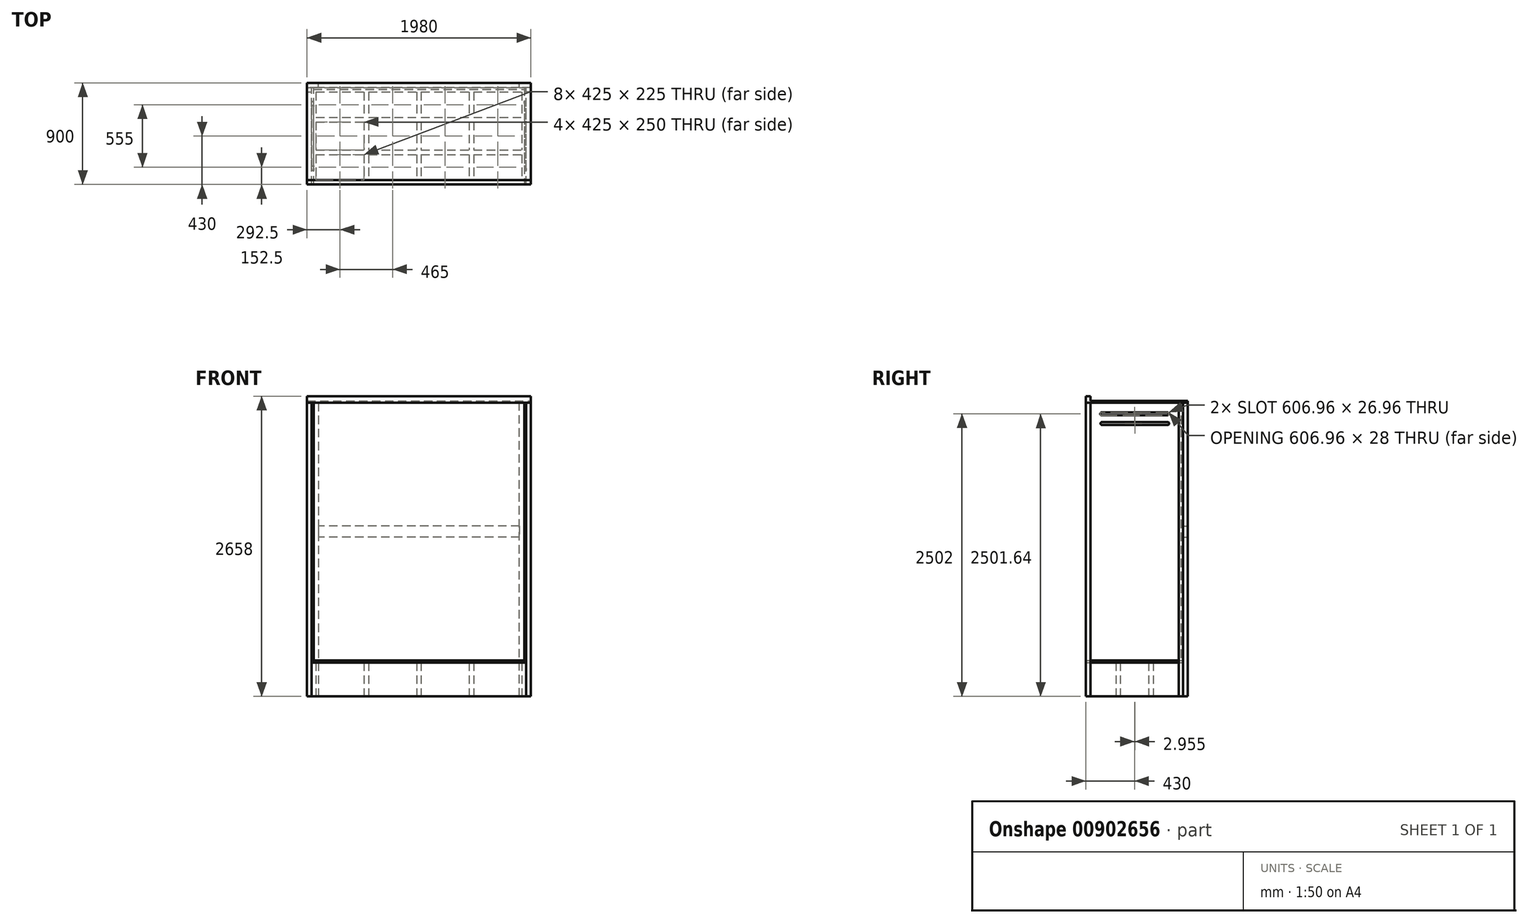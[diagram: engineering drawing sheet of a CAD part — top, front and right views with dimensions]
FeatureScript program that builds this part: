
annotation { "Feature Type Name" : "Feature", "Feature Type Description" : "" }
export const myFeature = defineFeature(function(context is Context, id is Id, definition is map)
    precondition{}
    {
        {
            var Q0;
            Q0=qCreatedBy(makeId("Top.planeOp"),FACE);
            var sketch = newSketch(context, id + "F0", { "sketchPlane" : qUnion([Q0])});
            skLineSegment(sketch, "E0.bottom", {"start": v(0, 0) * mm, "end": v(1900, 0) * mm});
            skLineSegment(sketch, "E0.top", {"start": v(0, 860) * mm, "end": v(1900, 860) * mm});
            skLineSegment(sketch, "E0.left", {"start": v(0, 0) * mm, "end": v(0, 860) * mm});
            skLineSegment(sketch, "E0.right", {"start": v(1900, 0) * mm, "end": v(1900, 860) * mm});
            skLineSegment(sketch, "E1.bottom", {"start": v(40, 820) * mm, "end": v(465, 820) * mm});
            skLineSegment(sketch, "E1.top", {"start": v(40, 40) * mm, "end": v(465, 40) * mm});
            skLineSegment(sketch, "E1.left", {"start": v(40, 820) * mm, "end": v(40, 595) * mm});
            skLineSegment(sketch, "E1.right", {"start": v(465, 820) * mm, "end": v(465, 595) * mm});
            skLineSegment(sketch, "E2.bottom", {"start": v(505, 820) * mm, "end": v(930, 820) * mm});
            skLineSegment(sketch, "E2.top", {"start": v(505, 40) * mm, "end": v(930, 40) * mm});
            skLineSegment(sketch, "E2.left", {"start": v(505, 820) * mm, "end": v(505, 595) * mm});
            skLineSegment(sketch, "E2.right", {"start": v(930, 820) * mm, "end": v(930, 595) * mm});
            skLineSegment(sketch, "E3.bottom", {"start": v(970, 820) * mm, "end": v(1395, 820) * mm});
            skLineSegment(sketch, "E3.top", {"start": v(970, 40) * mm, "end": v(1395, 40) * mm});
            skLineSegment(sketch, "E3.left", {"start": v(970, 820) * mm, "end": v(970, 595) * mm});
            skLineSegment(sketch, "E3.right", {"start": v(1395, 820) * mm, "end": v(1395, 595) * mm});
            skLineSegment(sketch, "E4.bottom", {"start": v(1435, 820) * mm, "end": v(1860, 820) * mm});
            skLineSegment(sketch, "E4.top", {"start": v(1435, 40) * mm, "end": v(1860, 40) * mm});
            skLineSegment(sketch, "E4.left", {"start": v(1435, 820) * mm, "end": v(1435, 595) * mm});
            skLineSegment(sketch, "E4.right", {"start": v(1860, 820) * mm, "end": v(1860, 595) * mm});
            skLineSegment(sketch, "E5.bottom", {"start": v(40, 595) * mm, "end": v(465, 595) * mm});
            skLineSegment(sketch, "E5.top", {"start": v(40, 555) * mm, "end": v(465, 555) * mm});
            skLineSegment(sketch, "E6.bottom", {"start": v(40, 265) * mm, "end": v(465, 265) * mm});
            skLineSegment(sketch, "E6.top", {"start": v(40, 305) * mm, "end": v(465, 305) * mm});
            skLineSegment(sketch, "E7.trimOffspring", {"start": v(505, 595) * mm, "end": v(930, 595) * mm});
            skLineSegment(sketch, "E8.trimOffspring", {"start": v(505, 555) * mm, "end": v(930, 555) * mm});
            skLineSegment(sketch, "E9.trimOffspring", {"start": v(465, 555) * mm, "end": v(465, 305) * mm});
            skLineSegment(sketch, "E10.trimOffspring", {"start": v(40, 555) * mm, "end": v(40, 305) * mm});
            skLineSegment(sketch, "E11.trimOffspring", {"start": v(505, 305) * mm, "end": v(930, 305) * mm});
            skLineSegment(sketch, "E12.trimOffspring", {"start": v(505, 265) * mm, "end": v(930, 265) * mm});
            skLineSegment(sketch, "E13.trimOffspring", {"start": v(970, 305) * mm, "end": v(1395, 305) * mm});
            skLineSegment(sketch, "E14.trimOffspring", {"start": v(970, 265) * mm, "end": v(1395, 265) * mm});
            skLineSegment(sketch, "E15.trimOffspring", {"start": v(970, 595) * mm, "end": v(1395, 595) * mm});
            skLineSegment(sketch, "E16.trimOffspring", {"start": v(970, 555) * mm, "end": v(1395, 555) * mm});
            skLineSegment(sketch, "E17.trimOffspring", {"start": v(1435, 595) * mm, "end": v(1860, 595) * mm});
            skLineSegment(sketch, "E18.trimOffspring", {"start": v(1435, 555) * mm, "end": v(1860, 555) * mm});
            skLineSegment(sketch, "E19.trimOffspring", {"start": v(1435, 305) * mm, "end": v(1860, 305) * mm});
            skLineSegment(sketch, "E20.trimOffspring", {"start": v(1435, 265) * mm, "end": v(1860, 265) * mm});
            skLineSegment(sketch, "E21.trimOffspring", {"start": v(505, 555) * mm, "end": v(505, 305) * mm});
            skLineSegment(sketch, "E22.trimOffspring", {"start": v(40, 265) * mm, "end": v(40, 40) * mm});
            skLineSegment(sketch, "E23.trimOffspring", {"start": v(465, 265) * mm, "end": v(465, 40) * mm});
            skLineSegment(sketch, "E24.trimOffspring", {"start": v(505, 265) * mm, "end": v(505, 40) * mm});
            skLineSegment(sketch, "E25.trimOffspring", {"start": v(930, 555) * mm, "end": v(930, 305) * mm});
            skLineSegment(sketch, "E26.trimOffspring", {"start": v(970, 555) * mm, "end": v(970, 305) * mm});
            skLineSegment(sketch, "E27.trimOffspring", {"start": v(970, 265) * mm, "end": v(970, 40) * mm});
            skLineSegment(sketch, "E28.trimOffspring", {"start": v(930, 265) * mm, "end": v(930, 40) * mm});
            skLineSegment(sketch, "E29.trimOffspring", {"start": v(1435, 265) * mm, "end": v(1435, 40) * mm});
            skLineSegment(sketch, "E30.trimOffspring", {"start": v(1395, 265) * mm, "end": v(1395, 40) * mm});
            skLineSegment(sketch, "E31.trimOffspring", {"start": v(1860, 265) * mm, "end": v(1860, 40) * mm});
            skLineSegment(sketch, "E32.trimOffspring", {"start": v(1860, 555) * mm, "end": v(1860, 305) * mm});
            skLineSegment(sketch, "E33.trimOffspring", {"start": v(1435, 555) * mm, "end": v(1435, 305) * mm});
            skLineSegment(sketch, "E34.trimOffspring", {"start": v(1395, 555) * mm, "end": v(1395, 305) * mm});
            skSolve(sketch);
        }
        {
            var Q0;
            Q0 = qSketchRegion(id + "F0", true);
            extrude(context, id + "F1", {"entities" : qUnion([Q0]), "depth" : 300 * mm, "offsetDistance" : 25 * mm});
        }
        {
            var Q0;
            Q0=makeQuery(id+"F1.opExtrude","CAP_FACE",FACE,{"disambiguationData":[OSD([sQuery(id+"F0.wireOp",EDGE,"E0.bottom"),sQuery(id+"F0.wireOp",EDGE,"E0.top"),sQuery(id+"F0.wireOp",EDGE,"E0.left"),sQuery(id+"F0.wireOp",EDGE,"E0.right"),sQuery(id+"F0.wireOp",EDGE,"E1.bottom"),sQuery(id+"F0.wireOp",EDGE,"E1.top"),sQuery(id+"F0.wireOp",EDGE,"E1.left"),sQuery(id+"F0.wireOp",EDGE,"E1.right"),sQuery(id+"F0.wireOp",EDGE,"E2.bottom"),sQuery(id+"F0.wireOp",EDGE,"E2.top"),sQuery(id+"F0.wireOp",EDGE,"E2.left"),sQuery(id+"F0.wireOp",EDGE,"E2.right"),sQuery(id+"F0.wireOp",EDGE,"E3.bottom"),sQuery(id+"F0.wireOp",EDGE,"E3.top"),sQuery(id+"F0.wireOp",EDGE,"E3.left"),sQuery(id+"F0.wireOp",EDGE,"E3.right"),sQuery(id+"F0.wireOp",EDGE,"E4.bottom"),sQuery(id+"F0.wireOp",EDGE,"E4.top"),sQuery(id+"F0.wireOp",EDGE,"E4.left"),sQuery(id+"F0.wireOp",EDGE,"E4.right"),sQuery(id+"F0.wireOp",EDGE,"E5.bottom"),sQuery(id+"F0.wireOp",EDGE,"E5.top"),sQuery(id+"F0.wireOp",EDGE,"E6.bottom"),sQuery(id+"F0.wireOp",EDGE,"E6.top"),sQuery(id+"F0.wireOp",EDGE,"E7.trimOffspring"),sQuery(id+"F0.wireOp",EDGE,"E8.trimOffspring"),sQuery(id+"F0.wireOp",EDGE,"E9.trimOffspring"),sQuery(id+"F0.wireOp",EDGE,"E10.trimOffspring"),sQuery(id+"F0.wireOp",EDGE,"E11.trimOffspring"),sQuery(id+"F0.wireOp",EDGE,"E12.trimOffspring"),sQuery(id+"F0.wireOp",EDGE,"E13.trimOffspring"),sQuery(id+"F0.wireOp",EDGE,"E14.trimOffspring"),sQuery(id+"F0.wireOp",EDGE,"E15.trimOffspring"),sQuery(id+"F0.wireOp",EDGE,"E16.trimOffspring"),sQuery(id+"F0.wireOp",EDGE,"E17.trimOffspring"),sQuery(id+"F0.wireOp",EDGE,"E18.trimOffspring"),sQuery(id+"F0.wireOp",EDGE,"E19.trimOffspring"),sQuery(id+"F0.wireOp",EDGE,"E20.trimOffspring"),sQuery(id+"F0.wireOp",EDGE,"E21.trimOffspring"),sQuery(id+"F0.wireOp",EDGE,"E22.trimOffspring"),sQuery(id+"F0.wireOp",EDGE,"E23.trimOffspring"),sQuery(id+"F0.wireOp",EDGE,"E24.trimOffspring"),sQuery(id+"F0.wireOp",EDGE,"E25.trimOffspring"),sQuery(id+"F0.wireOp",EDGE,"E26.trimOffspring"),sQuery(id+"F0.wireOp",EDGE,"E27.trimOffspring"),sQuery(id+"F0.wireOp",EDGE,"E28.trimOffspring"),sQuery(id+"F0.wireOp",EDGE,"E29.trimOffspring"),sQuery(id+"F0.wireOp",EDGE,"E30.trimOffspring"),sQuery(id+"F0.wireOp",EDGE,"E31.trimOffspring"),sQuery(id+"F0.wireOp",EDGE,"E32.trimOffspring"),sQuery(id+"F0.wireOp",EDGE,"E33.trimOffspring"),sQuery(id+"F0.wireOp",EDGE,"E34.trimOffspring")])],"isStart":false});
            var sketch = newSketch(context, id + "F2", { "sketchPlane" : qUnion([Q0])});
            skLineSegment(sketch, "E35.bottom", {"start": v(0, 860) * mm, "end": v(1900, 860) * mm});
            skLineSegment(sketch, "E35.top", {"start": v(0, 0) * mm, "end": v(1900, 0) * mm});
            skLineSegment(sketch, "E35.left", {"start": v(0, 860) * mm, "end": v(0, 0) * mm});
            skLineSegment(sketch, "E35.right", {"start": v(1900, 860) * mm, "end": v(1900, 0) * mm});
            skSolve(sketch);
        }
        {
            var Q0;
            Q0 = qSketchRegion(id + "F2", true);
            extrude(context, id + "F3", {"entities" : qUnion([Q0]), "depth" : 18 * mm, "offsetDistance" : 25 * mm});
        }
        {
            var Q0;
            Q0=makeQuery(id+"F1.opExtrude","SWEPT_FACE",FACE,{"disambiguationData":[OSD([sQuery(id+"F0.wireOp",EDGE,"E0.left")])]});
            var sketch = newSketch(context, id + "F4", { "sketchPlane" : qUnion([Q0])});
            skLineSegment(sketch, "E36.bottom", {"start": v(-860, 0) * mm, "end": v(-820, 0) * mm});
            skLineSegment(sketch, "E36.top", {"start": v(-860, 2600) * mm, "end": v(-820, 2600) * mm});
            skLineSegment(sketch, "E36.left", {"start": v(-860, 0) * mm, "end": v(-860, 2600) * mm});
            skLineSegment(sketch, "E36.right", {"start": v(-820, 0) * mm, "end": v(-820, 2600) * mm});
            skLineSegment(sketch, "E37.bottom", {"start": v(0, 0) * mm, "end": v(-40, 0) * mm});
            skLineSegment(sketch, "E37.top", {"start": v(0, 2600) * mm, "end": v(-40, 2600) * mm});
            skLineSegment(sketch, "E37.left", {"start": v(0, 0) * mm, "end": v(0, 2600) * mm});
            skLineSegment(sketch, "E37.right", {"start": v(-40, 0) * mm, "end": v(-40, 2600) * mm});
            skSolve(sketch);
        }
        {
            var Q0;
            Q0 = qSketchRegion(id + "F4", true);
            extrude(context, id + "F5", {"entities" : qUnion([Q0]), "depth" : 40 * mm, "offsetDistance" : 25 * mm});
        }
        {
            var Q0;
            Q0=makeQuery(id+"F5.opExtrude","CAP_FACE",FACE,{"disambiguationData":[OSD([sQuery(id+"F4.wireOp",EDGE,"E37.bottom"),sQuery(id+"F4.wireOp",EDGE,"E37.top"),sQuery(id+"F4.wireOp",EDGE,"E37.left"),sQuery(id+"F4.wireOp",EDGE,"E37.right")])],"isStart":true});
            var sketch = newSketch(context, id + "F6", { "sketchPlane" : qUnion([Q0])});
            skLineSegment(sketch, "E38.bottom", {"start": v(0, 2600) * mm, "end": v(860, 2600) * mm});
            skLineSegment(sketch, "E38.top", {"start": v(0, 318) * mm, "end": v(860, 318) * mm});
            skLineSegment(sketch, "E38.left", {"start": v(0, 2600) * mm, "end": v(0, 318) * mm});
            skLineSegment(sketch, "E38.right", {"start": v(860, 2600) * mm, "end": v(860, 318) * mm});
            skSolve(sketch);
        }
        {
            var Q0;
            Q0 = qSketchRegion(id + "F6", true);
            extrude(context, id + "F7", {"entities" : qUnion([Q0]), "depth" : 18 * mm, "offsetDistance" : 25 * mm});
        }
        {
            var Q0;
            Q0=makeQuery(id+"F1.opExtrude","SWEPT_FACE",FACE,{"disambiguationData":[OSD([sQuery(id+"F0.wireOp",EDGE,"E0.right")])]});
            var sketch = newSketch(context, id + "F8", { "sketchPlane" : qUnion([Q0])});
            skLineSegment(sketch, "E39.bottom", {"start": v(0, 0) * mm, "end": v(40, 0) * mm});
            skLineSegment(sketch, "E39.top", {"start": v(0, 2600) * mm, "end": v(40, 2600) * mm});
            skLineSegment(sketch, "E39.left", {"start": v(0, 0) * mm, "end": v(0, 2600) * mm});
            skLineSegment(sketch, "E39.right", {"start": v(40, 0) * mm, "end": v(40, 2600) * mm});
            skLineSegment(sketch, "E40.bottom", {"start": v(860, 0) * mm, "end": v(820, 0) * mm});
            skLineSegment(sketch, "E40.top", {"start": v(860, 2600) * mm, "end": v(820, 2600) * mm});
            skLineSegment(sketch, "E40.left", {"start": v(860, 0) * mm, "end": v(860, 2600) * mm});
            skLineSegment(sketch, "E40.right", {"start": v(820, 0) * mm, "end": v(820, 2600) * mm});
            skSolve(sketch);
        }
        {
            var Q0;
            Q0 = qSketchRegion(id + "F8", true);
            extrude(context, id + "F9", {"entities" : qUnion([Q0]), "depth" : 40 * mm, "offsetDistance" : 25 * mm});
        }
        {
            var Q0;
            Q0=makeQuery(id+"F9.opExtrude","CAP_FACE",FACE,{"disambiguationData":[OSD([sQuery(id+"F8.wireOp",EDGE,"E40.bottom"),sQuery(id+"F8.wireOp",EDGE,"E40.top"),sQuery(id+"F8.wireOp",EDGE,"E40.left"),sQuery(id+"F8.wireOp",EDGE,"E40.right")])],"isStart":true});
            var sketch = newSketch(context, id + "F10", { "sketchPlane" : qUnion([Q0])});
            skLineSegment(sketch, "E41.bottom", {"start": v(-860, 2600) * mm, "end": v(0, 2600) * mm});
            skLineSegment(sketch, "E41.top", {"start": v(-860, 318) * mm, "end": v(0, 318) * mm});
            skLineSegment(sketch, "E41.left", {"start": v(-860, 2600) * mm, "end": v(-860, 318) * mm});
            skLineSegment(sketch, "E41.right", {"start": v(0, 2600) * mm, "end": v(0, 318) * mm});
            skSolve(sketch);
        }
        {
            var Q0;
            Q0 = qSketchRegion(id + "F10", true);
            extrude(context, id + "F11", {"entities" : qUnion([Q0]), "depth" : 18 * mm, "offsetDistance" : 25 * mm});
        }
        {
            var Q0;
            Q0=makeQuery(id+"F9.opExtrude","SWEPT_FACE",FACE,{"disambiguationData":[OSD([sQuery(id+"F8.wireOp",EDGE,"E40.left")])]});
            var sketch = newSketch(context, id + "F12", { "sketchPlane" : qUnion([Q0])});
            skLineSegment(sketch, "E42.bottom", {"start": v(-1940, 0) * mm, "end": v(-1840, 0) * mm});
            skLineSegment(sketch, "E42.top", {"start": v(-1940, 2600) * mm, "end": v(-1840, 2600) * mm});
            skLineSegment(sketch, "E42.left", {"start": v(-1940, 0) * mm, "end": v(-1940, 2600) * mm});
            skLineSegment(sketch, "E42.right", {"start": v(40, 0) * mm, "end": v(40, 2600) * mm});
            skLineSegment(sketch, "E43", {"start": v(-1840, 0) * mm, "end": v(-1840, 2600) * mm});
            skLineSegment(sketch, "E44", {"start": v(-60, 2600) * mm, "end": v(-60, 0) * mm});
            skLineSegment(sketch, "E45.trimOffspring", {"start": v(-60, 2600) * mm, "end": v(40, 2600) * mm});
            skLineSegment(sketch, "E46.trimOffspring", {"start": v(-60, 0) * mm, "end": v(40, 0) * mm});
            skSolve(sketch);
        }
        {
            var Q0;
            Q0 = qSketchRegion(id + "F12", true);
            extrude(context, id + "F13", {"entities" : qUnion([Q0]), "depth" : 40 * mm, "offsetDistance" : 25 * mm});
        }
        {
            var Q0;
            Q0=makeQuery(id+"F13.opExtrude","CAP_FACE",FACE,{"disambiguationData":[OSD([sQuery(id+"F12.wireOp",EDGE,"E42.right"),sQuery(id+"F12.wireOp",EDGE,"E44"),sQuery(id+"F12.wireOp",EDGE,"E45.trimOffspring"),sQuery(id+"F12.wireOp",EDGE,"E46.trimOffspring")])],"isStart":true});
            var sketch = newSketch(context, id + "F14", { "sketchPlane" : qUnion([Q0])});
            skLineSegment(sketch, "E47", {"start": v(-40, 2600) * mm, "end": v(18, 2600) * mm, "construction": true});
            skLineSegment(sketch, "E48.bottom", {"start": v(18, 2600) * mm, "end": v(1892, 2600) * mm});
            skLineSegment(sketch, "E48.top", {"start": v(18, 318) * mm, "end": v(1892, 318) * mm});
            skLineSegment(sketch, "E48.left", {"start": v(18, 2600) * mm, "end": v(18, 318) * mm});
            skLineSegment(sketch, "E48.right", {"start": v(1892, 2600) * mm, "end": v(1892, 318) * mm});
            skSolve(sketch);
        }
        {
            var Q0;
            Q0 = qSketchRegion(id + "F14", true);
            extrude(context, id + "F15", {"entities" : qUnion([Q0]), "depth" : 18 * mm, "offsetDistance" : 25 * mm});
        }
        {
            var Q0;
            Q0=makeQuery(id+"F13.opExtrude","SWEPT_FACE",FACE,{"disambiguationData":[OSD([sQuery(id+"F12.wireOp",EDGE,"E45.trimOffspring")])]});
            var sketch = newSketch(context, id + "F16", { "sketchPlane" : qUnion([Q0])});
            skLineSegment(sketch, "E49.bottom", {"start": v(-40, 900) * mm, "end": v(1940, 900) * mm});
            skLineSegment(sketch, "E49.top", {"start": v(-40, 0) * mm, "end": v(1940, 0) * mm});
            skLineSegment(sketch, "E49.left", {"start": v(-40, 900) * mm, "end": v(-40, 0) * mm});
            skLineSegment(sketch, "E49.right", {"start": v(1940, 900) * mm, "end": v(1940, 0) * mm});
            skSolve(sketch);
        }
        {
            var Q0;
            Q0 = qSketchRegion(id + "F16", true);
            extrude(context, id + "F17", {"entities" : qUnion([Q0]), "depth" : 18 * mm, "offsetDistance" : 25 * mm});
        }
        {
            var Q0;
            Q0=makeQuery(id+"F13.opExtrude","SWEPT_FACE",FACE,{"disambiguationData":[OSD([sQuery(id+"F12.wireOp",EDGE,"E44")])]});
            var sketch = newSketch(context, id + "F18", { "sketchPlane" : qUnion([Q0])});
            skLineSegment(sketch, "E50.bottom", {"start": v(860, 1510) * mm, "end": v(900, 1510) * mm});
            skLineSegment(sketch, "E50.top", {"start": v(860, 1410) * mm, "end": v(900, 1410) * mm});
            skLineSegment(sketch, "E50.left", {"start": v(860, 1510) * mm, "end": v(860, 1410) * mm});
            skLineSegment(sketch, "E50.right", {"start": v(900, 1510) * mm, "end": v(900, 1410) * mm});
            skSolve(sketch);
        }
        {
            var Q0;
            Q0 = qSketchRegion(id + "F18", true);
            extrude(context, id + "F19", {"entities" : qUnion([Q0]), "endBound" : BoundingType.UP_TO_NEXT, "depth" : 25 * mm, "offsetDistance" : 25 * mm});
        }
        {
            var Q0;
            Q0=makeQuery(id+"F17.opExtrude","SWEPT_FACE",FACE,{"disambiguationData":[OSD([sQuery(id+"F16.wireOp",EDGE,"E49.right")])]});
            var sketch = newSketch(context, id + "F20", { "sketchPlane" : qUnion([Q0])});
            skLineSegment(sketch, "E51.bottom", {"start": v(0, 2618) * mm, "end": v(40, 2618) * mm});
            skLineSegment(sketch, "E51.top", {"start": v(0, 2658) * mm, "end": v(40, 2658) * mm});
            skLineSegment(sketch, "E51.left", {"start": v(0, 2618) * mm, "end": v(0, 2658) * mm});
            skLineSegment(sketch, "E51.right", {"start": v(40, 2618) * mm, "end": v(40, 2658) * mm});
            skSolve(sketch);
        }
        {
            var Q0;
            Q0 = qSketchRegion(id + "F20", true);
            extrude(context, id + "F21", {"entities" : qUnion([Q0]), "operationType" : NewBodyOperationType.ADD, "oppositeDirection" : true, "depth" : 1980 * mm, "offsetDistance" : 25 * mm});
        }
        {
            var Q0;
            Q0=makeQuery(id+"F11.opExtrude","CAP_FACE",FACE,{"disambiguationData":[OSD([sQuery(id+"F10.wireOp",EDGE,"E41.bottom"),sQuery(id+"F10.wireOp",EDGE,"E41.top"),sQuery(id+"F10.wireOp",EDGE,"E41.left"),sQuery(id+"F10.wireOp",EDGE,"E41.right")])],"isStart":true});
            var sketch = newSketch(context, id + "F22", { "sketchPlane" : qUnion([Q0])});
            skLineSegment(sketch, "E52.bottom", {"start": v(140, 2488.17) * mm, "end": v(720, 2488.17) * mm});
            skLineSegment(sketch, "E52.top", {"start": v(140, 2515.12) * mm, "end": v(720, 2515.12) * mm});
            skArc(sketch, "E53", {"start": v(140, 2515.12) * mm, "mid": v(126.52, 2501.64) * mm, "end": v(140, 2488.17) * mm});
            skArc(sketch, "E54", {"start": v(720, 2488.17) * mm, "mid": v(733.48, 2501.64) * mm, "end": v(720, 2515.12) * mm});
            skLineSegment(sketch, "E55.bottom", {"start": v(142.96, 2403.25) * mm, "end": v(722.96, 2403.25) * mm});
            skLineSegment(sketch, "E55.top", {"start": v(142.96, 2430.2) * mm, "end": v(722.96, 2430.2) * mm});
            skArc(sketch, "E56", {"start": v(142.96, 2430.2) * mm, "mid": v(129.48, 2416.73) * mm, "end": v(142.96, 2403.25) * mm});
            skArc(sketch, "E57", {"start": v(722.96, 2403.25) * mm, "mid": v(736.43, 2416.73) * mm, "end": v(722.96, 2430.2) * mm});
            skSolve(sketch);
        }
        {
            var Q0;
            Q0 = qSketchRegion(id + "F22", true);
            extrude(context, id + "F23", {"entities" : qUnion([Q0]), "operationType" : NewBodyOperationType.REMOVE, "endBound" : BoundingType.THROUGH_ALL, "oppositeDirection" : true, "depth" : 25 * mm, "offsetDistance" : 25 * mm});
        }
        {
            var Q0;
            Q0=makeQuery(id+"F7.opExtrude","CAP_FACE",FACE,{"disambiguationData":[OSD([sQuery(id+"F6.wireOp",EDGE,"E38.bottom"),sQuery(id+"F6.wireOp",EDGE,"E38.top"),sQuery(id+"F6.wireOp",EDGE,"E38.left"),sQuery(id+"F6.wireOp",EDGE,"E38.right")])],"isStart":true});
            var sketch = newSketch(context, id + "F24", { "sketchPlane" : qUnion([Q0])});
            skLineSegment(sketch, "E58.bottom", {"start": v(-693.86, 2516) * mm, "end": v(-166.14, 2516) * mm});
            skLineSegment(sketch, "E58.top", {"start": v(-693.86, 2488) * mm, "end": v(-166.14, 2488) * mm});
            skLineSegment(sketch, "E59.bottom", {"start": v(-693.86, 2430) * mm, "end": v(-166.14, 2430) * mm});
            skLineSegment(sketch, "E59.top", {"start": v(-693.86, 2402) * mm, "end": v(-166.14, 2402) * mm});
            skArc(sketch, "E60", {"start": v(-693.86, 2516) * mm, "mid": v(-707.86, 2502) * mm, "end": v(-693.86, 2488) * mm});
            skArc(sketch, "E61", {"start": v(-693.86, 2430) * mm, "mid": v(-707.86, 2416) * mm, "end": v(-693.86, 2402) * mm});
            skArc(sketch, "E62", {"start": v(-166.14, 2402) * mm, "mid": v(-152.14, 2416) * mm, "end": v(-166.14, 2430) * mm});
            skArc(sketch, "E63", {"start": v(-166.14, 2488) * mm, "mid": v(-152.14, 2502) * mm, "end": v(-166.14, 2516) * mm});
            skSolve(sketch);
        }
        {
            var Q0;
            Q0 = qSketchRegion(id + "F24", true);
            extrude(context, id + "F25", {"entities" : qUnion([Q0]), "operationType" : NewBodyOperationType.REMOVE, "oppositeDirection" : true, "depth" : 25 * mm, "offsetDistance" : 25 * mm});
        }
    });
